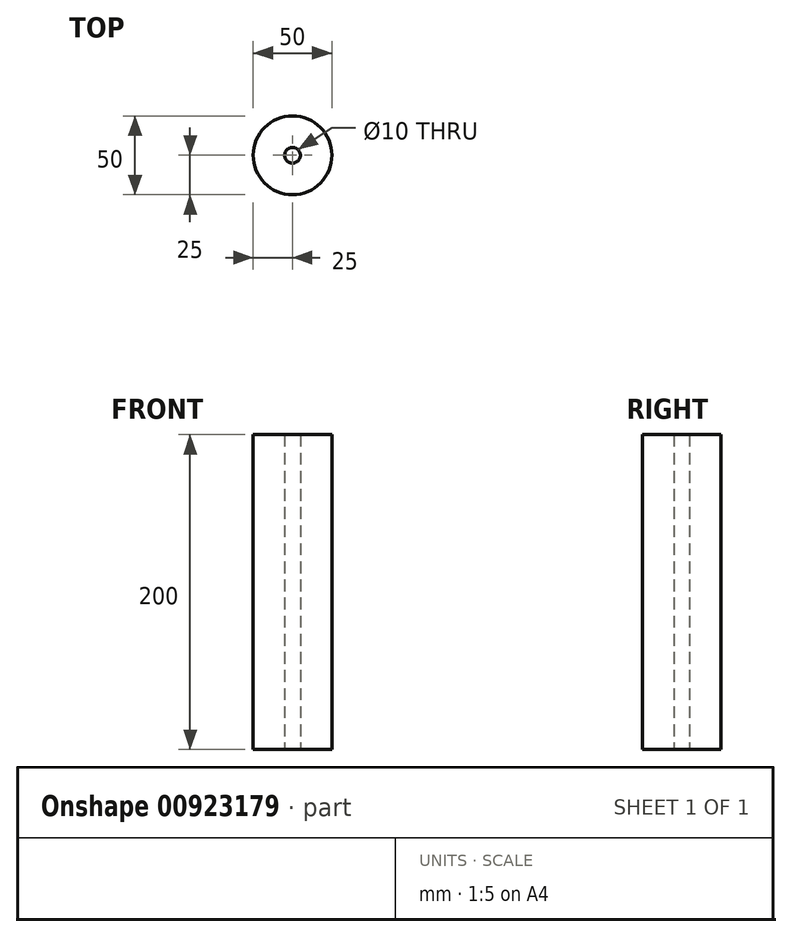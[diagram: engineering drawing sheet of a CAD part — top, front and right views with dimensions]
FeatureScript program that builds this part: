
annotation { "Feature Type Name" : "Feature", "Feature Type Description" : "" }
export const myFeature = defineFeature(function(context is Context, id is Id, definition is map)
    precondition{}
    {
        {
            var Q0;
            Q0=qCreatedBy(makeId("Top.planeOp"),FACE);
            var sketch = newSketch(context, id + "F0", { "sketchPlane" : qUnion([Q0])});
            skCircle(sketch, "E0", {"center": v(0, 0) * mm, "radius": 25 * mm});
            skCircle(sketch, "E1", {"center": v(0, 0) * mm, "radius": 5 * mm});
            skSolve(sketch);
        }
        {
            var Q0;
            Q0=makeQuery(id+"F0.imprint","IMPRINT",FACE,{"disambiguationData":[TD([[makeQuery(id+"F0.imprint","IMPRINT",EDGE,{"derivedFrom":sQuery(id+"F0.wireOp",EDGE,"E0")}),1.0]])]});
            extrude(context, id + "F1", {"entities" : qUnion([Q0]), "depth" : 200 * mm, "offsetDistance" : 25 * mm});
        }
        {
            var Q0;
            Q0=makeQuery(id+"F0.imprint","IMPRINT",FACE,{"disambiguationData":[TD([[makeQuery(id+"F0.imprint","IMPRINT",EDGE,{"derivedFrom":sQuery(id+"F0.wireOp",EDGE,"E1")}),1.0]])]});
            extrude(context, id + "F2", {"entities" : qUnion([Q0]), "operationType" : NewBodyOperationType.REMOVE, "depth" : 200 * mm, "offsetDistance" : 25 * mm});
        }
    });
